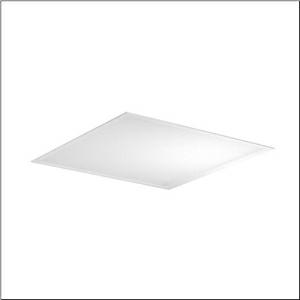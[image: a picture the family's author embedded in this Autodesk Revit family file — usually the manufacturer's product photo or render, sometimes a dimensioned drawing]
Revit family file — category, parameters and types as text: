
# Revit family: apollon_21_square_51mq12w72414
name_source: partatom
category: Lighting Fixtures
units: mm (PartAtom-declared; Revit-internal decimal feet)

## family parameters
Cut with Voids When Loaded = No
Host = Face
Light Source = No
Part Type = Normal
Room Calculation Point = No
Round Connector Dimension = Use Diameter
Shared = No

## types (1)
- Apollon 21 square (1 x LED, 4200 lm, 23.3 W, 4000K)
    Apparent Load = 23 VA
    CIE Flux Codes = 60 87 97 100 100
    Color Rendering = 80
    Color Temperature = 4000K
    Default Elevation = 1800 mm
    Description = Apollon 21 square, office luminaire, primary optical cover: micro prismatic cover, of PMMA, CAT 2 (L<= 3000cd/m²), light emission: direct distribution, primary light characteristic: symmetric, installation type: lay-in mounting, LED, rated luminous flux: 4.200lm, luminous efficacy: 180lm/W, light colour: 840, colour temperature: 4000K, control gear: ON/OFF, with terminal, 3-pole, mains connection: 220..240V, AC/DC, 0/50..60Hz, rated input power: 23W, suitable for self-contained emergency lighting element 59MQE002602A with integrated self-test function according to EN 60598-2-22, housing, of aluminium, coated, traffic white (RAL 9016), module: M600, length: 595mm, width: 595mm, height: 55mm, recess depth: 180mm, housing upper side, of sheet steel, galvanised, protection rating (complete): IP20, protection rating (lamp compartment, on room side): IP50, insulation class (complete): insulation class II (safety insulation), certification: CE, ENEC, impact resistance: IK03, permissible operating ambient temperature: -20..+45°C, permissible storage temperature: -40..+80°C, standard: EN 60598-2-22, packaging unit: 1 piece
    Height = 0 mm  [stored 0 ft]
    Lamp = 1 x LED
    Lamp Light Flux = 4200 lm
    Lamp Power = 23.3 W
    Lamp count = 1
    Length = 595 mm
    Luminous efficacy = 180 lm/W
    Manufacturer = Siteco
    ModVariant = No
    Model = 51MQ12W72414
    Mounting Place = Ceiling
    Mounting Type = Recessed
    Number of Poles = 1
    OnlyDefault = Yes
    Power Factor = 1
    Product Name = Apollon 21 square
    Product group = office luminaire | ceiling recessed
    ProductGroupID = 400
    Protection Class = Protection class II
    Protection Degree = IP 20
    RLX_Detail_Level = 1
    RLX_Emergency_Light_Flux = 0 lm
    RLX_Emergency_Type = 0
    RLX_Emergency_Type_DB = No
    RlxData = <blob elided: 12697 chars, md5=9aa3988f>
    Socket = socket
    Standby Power = 0 W
    System Light Flux = 4200 lm
    System Power = 23 W
    Type Comments = Product without accessories
    Type Image = l_1291049.jpg
    URL = http://relux.com
    VarID = ---
    Voltage = 0 V
    Weight = 0.00 kg
    Width = 595 mm

note: [stored X ft] marks values corroborated as IEEE doubles in the binary element streams (Revit-internal decimal feet)

## geometry (parser evidence)
native form markers: Sweep x8
no freeform markers — native parametric forms only
